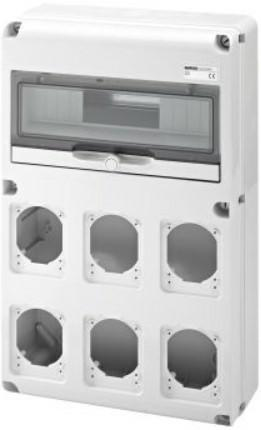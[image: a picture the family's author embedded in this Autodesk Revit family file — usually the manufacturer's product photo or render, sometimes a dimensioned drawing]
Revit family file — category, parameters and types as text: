
# Revit family: Building-QuadriIEC309-GEWISS-68QDIN-QUADRI-PRESE-14MOD_6PRESE
name_source: partatom
category: Apparecchi elettrici
units: mm (PartAtom-declared; Revit-internal decimal feet)

## family parameters
Condiviso = No
Host = Superficie
Mantenere orientamento annotazione = Sì
Punto di calcolo locali = Sì
Quota connettore circolare = Usa diametro
Taglio con vuoti quando caricato = No
Tipo di parte = Normale

## types (1)
- GW68008N - Q-DIN 14M 6FLANGE PR.16/32A IP65
    Catalogo = BUILDING
    Catalogo Serie = 68 QDIN
    Classe isolamento = II
    Codice EAN = 8011564744790
    Codice Electrocod = 2242
    Colore = Grigio RAL 7035
    Conformità normativa = EN 60208 - EN 60670-1 - IEC 60670-24
    Descrizione = Q-DIN 14M 6FLANGE PR.16/32A IP65
    Glow Wire Test = 650°C
    Grado di protezione = IP65
    IDF = 274be3b8-c24e-43b0-b35a-d88e7745b8e9
    IDT = cecb3bd3-e102-49fc-acd3-cb7b24533741
    Immagine tipo = GW68008N.jpg
    Modello = GW68008N
    N. coperchi ciechi in dotazione = 2 IEC 16/32 A
    N. mod. EN 50022 = 14
    N. prese alloggiabili = 6 IEC 309 16/32 A IP44/67
    POMELLO = bianco
    PRESA = rosso
    Potenza dissipabile A (W) = 24
    Potenza dissipabile B (W) = 64
    Produttore = GEWISS S.p.A.
    Prospetto di default = 1219 mm
    Resistenza agli urti = IK08
    SEO = Quadretto
    STRUTTURA = RAL - 7035
    STRUTTURA ALTA = Poche
    Scheda Tecnica = https://www.gewiss.com
    Spostamento_S = 1000 mm  [stored 3.28084 ft]
    Temperatura di utilizzo = -25 +40 °C
    Termopressione con biglia = 70 °C
    Tipo versione = Vuoto
    Tipologia di installazione = Da parete
    URL = https://www.gewiss.com
    VETRO = Vetro
    Versione file RFA = 21.5

note: [stored X ft] marks values corroborated as IEEE doubles in the binary element streams (Revit-internal decimal feet)

## geometry (parser evidence)
native form markers: Sweep x4
no freeform markers — native parametric forms only
